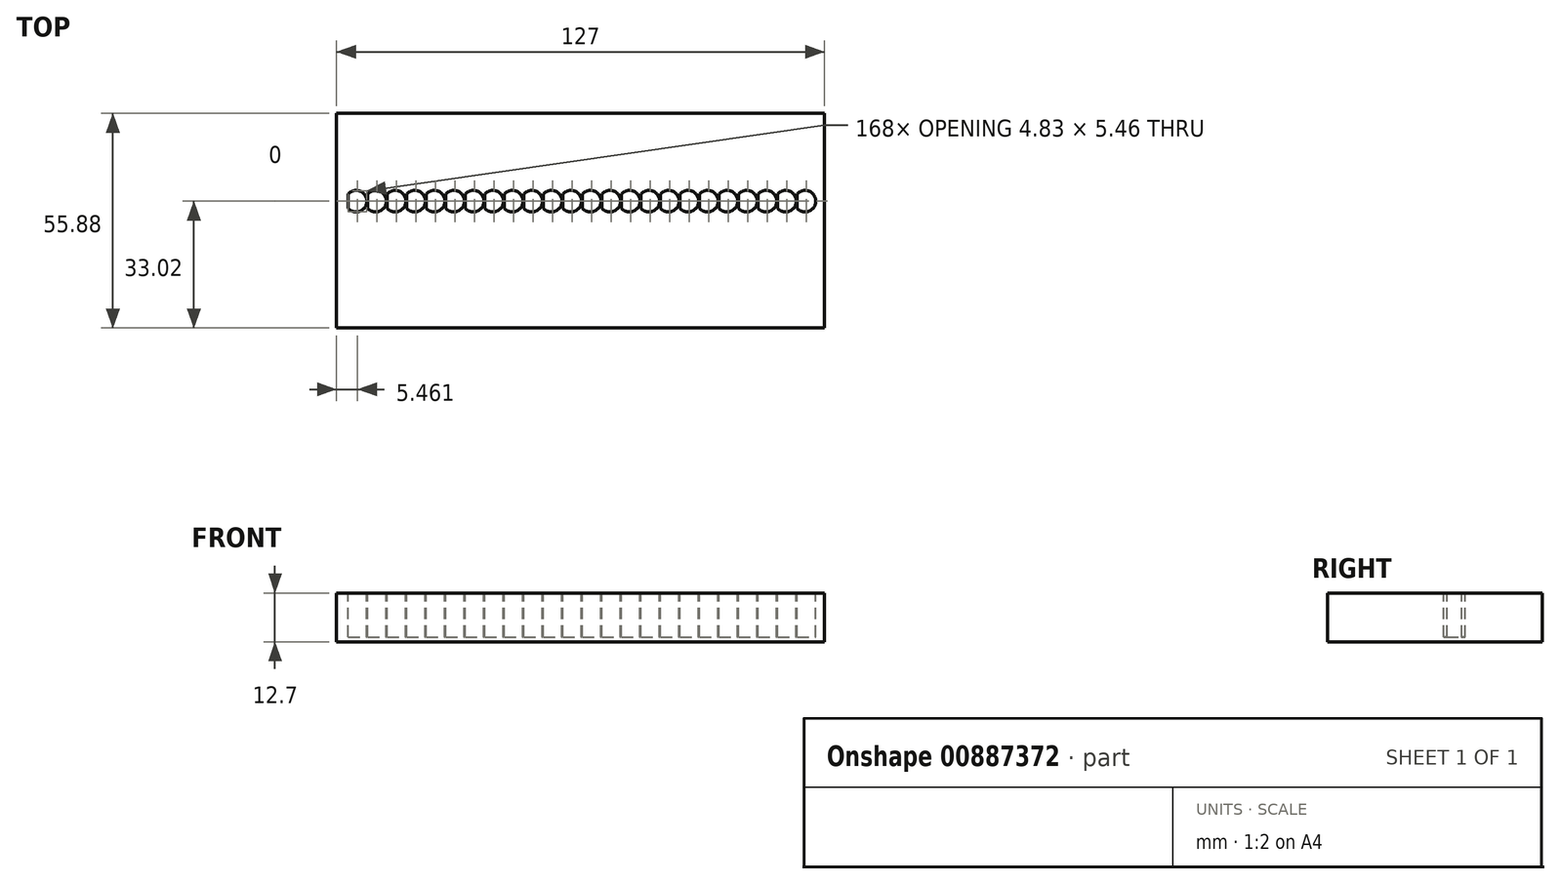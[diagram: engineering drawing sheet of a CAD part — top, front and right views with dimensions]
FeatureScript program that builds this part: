
annotation { "Feature Type Name" : "Feature", "Feature Type Description" : "" }
export const myFeature = defineFeature(function(context is Context, id is Id, definition is map)
    precondition{}
    {
        {
            var Q0;
            Q0=qCreatedBy(makeId("Top.planeOp"),FACE);
            var sketch = newSketch(context, id + "F0", { "sketchPlane" : qUnion([Q0])});
            skLineSegment(sketch, "E0.bottom", {"start": v(-63.5, 27.94) * mm, "end": v(63.5, 27.94) * mm});
            skLineSegment(sketch, "E0.top", {"start": v(-63.5, -27.94) * mm, "end": v(63.5, -27.94) * mm});
            skLineSegment(sketch, "E0.left", {"start": v(-63.5, 27.94) * mm, "end": v(-63.5, -27.94) * mm});
            skLineSegment(sketch, "E0.right", {"start": v(63.5, 27.94) * mm, "end": v(63.5, -27.94) * mm});
            skSolve(sketch);
        }
        {
            var Q0;
            Q0 = qSketchRegion(id + "F0", true);
            extrude(context, id + "F1", {"entities" : qUnion([Q0]), "depth" : 12.7 * mm, "offsetDistance" : 25.4 * mm});
        }
        {
            var Q0;
            Q0=makeQuery(id+"F1.opExtrude","CAP_FACE",FACE,{"disambiguationData":[OSD([sQuery(id+"F0.wireOp",EDGE,"E0.bottom"),sQuery(id+"F0.wireOp",EDGE,"E0.top"),sQuery(id+"F0.wireOp",EDGE,"E0.left"),sQuery(id+"F0.wireOp",EDGE,"E0.right")])],"isStart":false});
            var sketch = newSketch(context, id + "F2", { "sketchPlane" : qUnion([Q0])});
            skArc(sketch, "E1", {"start": v(-60.45, 3.16) * mm, "mid": v(-55.63, 5.08) * mm, "end": v(-60.45, 7) * mm});
            skLineSegment(sketch, "E2.right", {"start": v(-60.45, 3.16) * mm, "end": v(-60.45, 7) * mm});
            skLineSegment(sketch, "E3", {"start": v(-55.63, 7.67) * mm, "end": v(-55.63, 1.83) * mm, "construction": true});
            skLineSegment(sketch, "E4.1.0.0", {"start": v(-55.37, 3.16) * mm, "end": v(-55.37, 7) * mm});
            skArc(sketch, "E4.1.0.1", {"start": v(-55.37, 3.16) * mm, "mid": v(-50.55, 5.08) * mm, "end": v(-55.37, 7) * mm});
            skLineSegment(sketch, "E4.2.0.0", {"start": v(-50.3, 3.16) * mm, "end": v(-50.3, 7) * mm});
            skArc(sketch, "E4.2.0.1", {"start": v(-50.3, 3.16) * mm, "mid": v(-45.47, 5.08) * mm, "end": v(-50.3, 7) * mm});
            skLineSegment(sketch, "E4.3.0.0", {"start": v(-45.21, 3.16) * mm, "end": v(-45.21, 7) * mm});
            skArc(sketch, "E4.3.0.1", {"start": v(-45.21, 3.16) * mm, "mid": v(-40.39, 5.08) * mm, "end": v(-45.21, 7) * mm});
            skLineSegment(sketch, "E4.4.0.0", {"start": v(-40.13, 3.16) * mm, "end": v(-40.13, 7) * mm});
            skArc(sketch, "E4.4.0.1", {"start": v(-40.13, 3.16) * mm, "mid": v(-35.3, 5.08) * mm, "end": v(-40.13, 7) * mm});
            skLineSegment(sketch, "E4.5.0.0", {"start": v(-35.05, 3.16) * mm, "end": v(-35.05, 7) * mm});
            skArc(sketch, "E4.5.0.1", {"start": v(-35.05, 3.16) * mm, "mid": v(-30.23, 5.08) * mm, "end": v(-35.05, 7) * mm});
            skLineSegment(sketch, "E4.6.0.0", {"start": v(-29.97, 3.16) * mm, "end": v(-29.97, 7) * mm});
            skArc(sketch, "E4.6.0.1", {"start": v(-29.97, 3.16) * mm, "mid": v(-25.15, 5.08) * mm, "end": v(-29.97, 7) * mm});
            skLineSegment(sketch, "E4.7.0.0", {"start": v(-24.9, 3.16) * mm, "end": v(-24.9, 7) * mm});
            skArc(sketch, "E4.7.0.1", {"start": v(-24.9, 3.16) * mm, "mid": v(-20.07, 5.08) * mm, "end": v(-24.9, 7) * mm});
            skLineSegment(sketch, "E4.8.0.0", {"start": v(-19.81, 3.16) * mm, "end": v(-19.81, 7) * mm});
            skArc(sketch, "E4.8.0.1", {"start": v(-19.81, 3.16) * mm, "mid": v(-14.99, 5.08) * mm, "end": v(-19.81, 7) * mm});
            skLineSegment(sketch, "E4.9.0.0", {"start": v(-14.73, 3.16) * mm, "end": v(-14.73, 7) * mm});
            skArc(sketch, "E4.9.0.1", {"start": v(-14.73, 3.16) * mm, "mid": v(-9.9, 5.08) * mm, "end": v(-14.73, 7) * mm});
            skLineSegment(sketch, "E4.10.0.0", {"start": v(-9.65, 3.16) * mm, "end": v(-9.65, 7) * mm});
            skArc(sketch, "E4.10.0.1", {"start": v(-9.65, 3.16) * mm, "mid": v(-4.83, 5.08) * mm, "end": v(-9.65, 7) * mm});
            skLineSegment(sketch, "E4.11.0.0", {"start": v(-4.57, 3.16) * mm, "end": v(-4.57, 7) * mm});
            skArc(sketch, "E4.11.0.1", {"start": v(-4.57, 3.16) * mm, "mid": v(0.25, 5.08) * mm, "end": v(-4.57, 7) * mm});
            skLineSegment(sketch, "E4.12.0.0", {"start": v(0.5, 3.16) * mm, "end": v(0.5, 7) * mm});
            skArc(sketch, "E4.12.0.1", {"start": v(0.5, 3.16) * mm, "mid": v(5.33, 5.08) * mm, "end": v(0.5, 7) * mm});
            skLineSegment(sketch, "E4.13.0.0", {"start": v(5.59, 3.16) * mm, "end": v(5.59, 7) * mm});
            skArc(sketch, "E4.13.0.1", {"start": v(5.59, 3.16) * mm, "mid": v(10.41, 5.08) * mm, "end": v(5.59, 7) * mm});
            skLineSegment(sketch, "E4.14.0.0", {"start": v(10.67, 3.16) * mm, "end": v(10.67, 7) * mm});
            skArc(sketch, "E4.14.0.1", {"start": v(10.67, 3.16) * mm, "mid": v(15.5, 5.08) * mm, "end": v(10.67, 7) * mm});
            skLineSegment(sketch, "E4.15.0.0", {"start": v(15.75, 3.16) * mm, "end": v(15.75, 7) * mm});
            skArc(sketch, "E4.15.0.1", {"start": v(15.75, 3.16) * mm, "mid": v(20.57, 5.08) * mm, "end": v(15.75, 7) * mm});
            skLineSegment(sketch, "E4.16.0.0", {"start": v(20.83, 3.16) * mm, "end": v(20.83, 7) * mm});
            skArc(sketch, "E4.16.0.1", {"start": v(20.83, 3.16) * mm, "mid": v(25.65, 5.08) * mm, "end": v(20.83, 7) * mm});
            skLineSegment(sketch, "E4.17.0.0", {"start": v(25.9, 3.16) * mm, "end": v(25.9, 7) * mm});
            skArc(sketch, "E4.17.0.1", {"start": v(25.9, 3.16) * mm, "mid": v(30.73, 5.08) * mm, "end": v(25.9, 7) * mm});
            skLineSegment(sketch, "E4.18.0.0", {"start": v(30.99, 3.16) * mm, "end": v(30.99, 7) * mm});
            skArc(sketch, "E4.18.0.1", {"start": v(30.99, 3.16) * mm, "mid": v(35.81, 5.08) * mm, "end": v(30.99, 7) * mm});
            skLineSegment(sketch, "E4.19.0.0", {"start": v(36.07, 3.16) * mm, "end": v(36.07, 7) * mm});
            skArc(sketch, "E4.19.0.1", {"start": v(36.07, 3.16) * mm, "mid": v(40.9, 5.08) * mm, "end": v(36.07, 7) * mm});
            skLineSegment(sketch, "E4.20.0.0", {"start": v(41.15, 3.16) * mm, "end": v(41.15, 7) * mm});
            skArc(sketch, "E4.20.0.1", {"start": v(41.15, 3.16) * mm, "mid": v(45.97, 5.08) * mm, "end": v(41.15, 7) * mm});
            skLineSegment(sketch, "E4.21.0.0", {"start": v(46.23, 3.16) * mm, "end": v(46.23, 7) * mm});
            skArc(sketch, "E4.21.0.1", {"start": v(46.23, 3.16) * mm, "mid": v(51.05, 5.08) * mm, "end": v(46.23, 7) * mm});
            skLineSegment(sketch, "E4.22.0.0", {"start": v(51.3, 3.16) * mm, "end": v(51.3, 7) * mm});
            skArc(sketch, "E4.22.0.1", {"start": v(51.3, 3.16) * mm, "mid": v(56.13, 5.08) * mm, "end": v(51.3, 7) * mm});
            skLineSegment(sketch, "E4.23.0.0", {"start": v(56.39, 3.16) * mm, "end": v(56.39, 7) * mm});
            skArc(sketch, "E4.23.0.1", {"start": v(56.39, 3.16) * mm, "mid": v(61.21, 5.08) * mm, "end": v(56.39, 7) * mm});
            skLineSegment(sketch, "E4.direction1", {"start": v(-60.45, 3.16) * mm, "end": v(-55.37, 3.16) * mm, "construction": true});
            skSolve(sketch);
        }
        {
            var Q0;
            Q0 = qSketchRegion(id + "F2", true);
            extrude(context, id + "F3", {"entities" : qUnion([Q0]), "operationType" : NewBodyOperationType.REMOVE, "oppositeDirection" : true, "depth" : 11.43 * mm, "offsetDistance" : 25.4 * mm});
        }
    });
